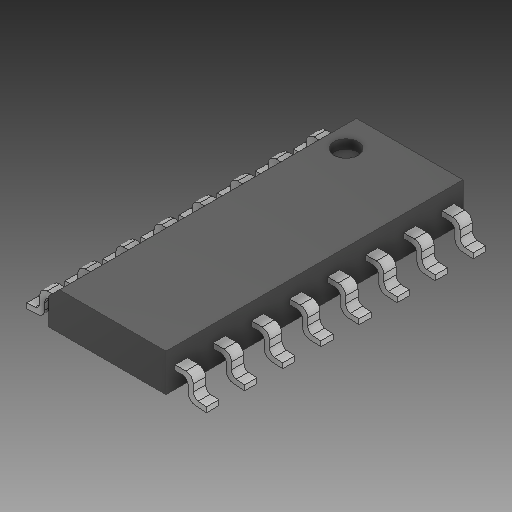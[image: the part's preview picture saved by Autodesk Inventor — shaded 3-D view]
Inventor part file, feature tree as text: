
AUTODESK INVENTOR PART (.ipt)
format: ipt  version: 2020 (Build 240168000, 168)  size: 248,832 bytes
history: native  units: mm
features: other x1, chamfer x1
ambient origin geometry x8: Origin, YZ Plane, XZ Plane, XY Plane, X Axis, Y Axis, Z Axis, Center Point
bodies: Body1 (feature_tree)
feature tree (2):
  other  "Твердое тело1"
  chamfer  "Chamfer1"  [1 undecoded]
note: 1 required parameter value undecoded (feature->parameter linkage not recoverable at this tier; creation-order binding heuristic only, values carry confidence <= 0.55)
